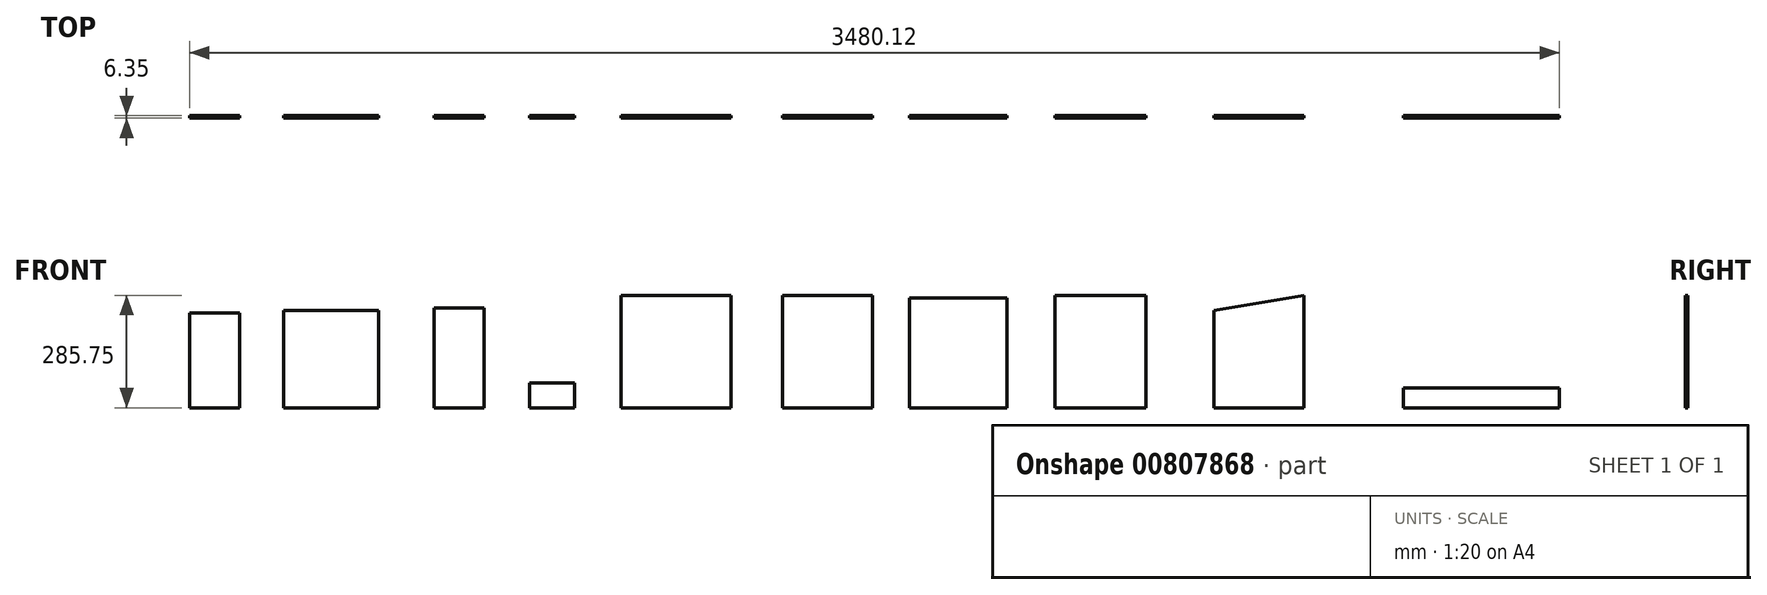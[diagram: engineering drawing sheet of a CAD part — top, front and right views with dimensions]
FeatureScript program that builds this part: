
annotation { "Feature Type Name" : "Feature", "Feature Type Description" : "" }
export const myFeature = defineFeature(function(context is Context, id is Id, definition is map)
    precondition{}
    {
        {
            var Q0;
            Q0=qCreatedBy(makeId("Front.planeOp"),FACE);
            var sketch = newSketch(context, id + "F0", { "sketchPlane" : qUnion([Q0])});
            skLineSegment(sketch, "E0.bottom", {"start": v(-480.49, 172.68) * mm, "end": v(-353.49, 172.68) * mm});
            skLineSegment(sketch, "E0.top", {"start": v(-480.49, -68.62) * mm, "end": v(-353.49, -68.62) * mm});
            skLineSegment(sketch, "E0.left", {"start": v(-480.49, 172.68) * mm, "end": v(-480.49, -68.62) * mm});
            skLineSegment(sketch, "E0.right", {"start": v(-353.49, 172.68) * mm, "end": v(-353.49, -68.62) * mm});
            skLineSegment(sketch, "E1.bottom", {"start": v(-241.3, 179.03) * mm, "end": v(0, 179.03) * mm});
            skLineSegment(sketch, "E1.top", {"start": v(-241.3, -68.62) * mm, "end": v(0, -68.62) * mm});
            skLineSegment(sketch, "E1.left", {"start": v(-241.3, 179.03) * mm, "end": v(-241.3, -68.62) * mm});
            skLineSegment(sketch, "E1.right", {"start": v(0, 179.03) * mm, "end": v(0, -68.62) * mm});
            skLineSegment(sketch, "E2.bottom", {"start": v(141.02, 185.38) * mm, "end": v(268.02, 185.38) * mm});
            skLineSegment(sketch, "E2.top", {"start": v(141.02, -68.62) * mm, "end": v(268.02, -68.62) * mm});
            skLineSegment(sketch, "E2.left", {"start": v(141.02, 185.38) * mm, "end": v(141.02, -68.62) * mm});
            skLineSegment(sketch, "E2.right", {"start": v(268.02, 185.38) * mm, "end": v(268.02, -68.62) * mm});
            skLineSegment(sketch, "E3.bottom", {"start": v(383.19, -68.62) * mm, "end": v(497.49, -68.62) * mm});
            skLineSegment(sketch, "E3.top", {"start": v(383.19, -5.12) * mm, "end": v(497.49, -5.12) * mm});
            skLineSegment(sketch, "E3.left", {"start": v(383.19, -68.62) * mm, "end": v(383.19, -5.12) * mm});
            skLineSegment(sketch, "E3.right", {"start": v(497.49, -68.62) * mm, "end": v(497.49, -5.12) * mm});
            skLineSegment(sketch, "E4.bottom", {"start": v(615.22, 217.13) * mm, "end": v(894.62, 217.13) * mm});
            skLineSegment(sketch, "E4.top", {"start": v(615.22, -68.62) * mm, "end": v(894.62, -68.62) * mm});
            skLineSegment(sketch, "E4.left", {"start": v(615.22, 217.13) * mm, "end": v(615.22, -68.62) * mm});
            skLineSegment(sketch, "E4.right", {"start": v(894.62, 217.13) * mm, "end": v(894.62, -68.62) * mm});
            skLineSegment(sketch, "E5.bottom", {"start": v(1026.44, 217.13) * mm, "end": v(1255.04, 217.13) * mm});
            skLineSegment(sketch, "E5.top", {"start": v(1026.44, -68.62) * mm, "end": v(1255.04, -68.62) * mm});
            skLineSegment(sketch, "E5.left", {"start": v(1026.44, 217.13) * mm, "end": v(1026.44, -68.62) * mm});
            skLineSegment(sketch, "E5.right", {"start": v(1255.04, 217.13) * mm, "end": v(1255.04, -68.62) * mm});
            skLineSegment(sketch, "E6.bottom", {"start": v(1347.93, 210.78) * mm, "end": v(1595.58, 210.78) * mm});
            skLineSegment(sketch, "E6.top", {"start": v(1347.93, -68.62) * mm, "end": v(1595.58, -68.62) * mm});
            skLineSegment(sketch, "E6.left", {"start": v(1347.93, 210.78) * mm, "end": v(1347.93, -68.62) * mm});
            skLineSegment(sketch, "E6.right", {"start": v(1595.58, 210.78) * mm, "end": v(1595.58, -68.62) * mm});
            skLineSegment(sketch, "E7.bottom", {"start": v(1717.51, 217.13) * mm, "end": v(1949.29, 217.13) * mm});
            skLineSegment(sketch, "E7.top", {"start": v(1717.51, -68.62) * mm, "end": v(1949.29, -68.62) * mm});
            skLineSegment(sketch, "E7.left", {"start": v(1717.51, 217.13) * mm, "end": v(1717.51, -68.62) * mm});
            skLineSegment(sketch, "E7.right", {"start": v(1949.29, 217.13) * mm, "end": v(1949.29, -68.62) * mm});
            skLineSegment(sketch, "E8.top", {"start": v(2121.79, -68.62) * mm, "end": v(2350.39, -68.62) * mm});
            skLineSegment(sketch, "E8.left", {"start": v(2121.79, 179.03) * mm, "end": v(2121.79, -68.62) * mm});
            skLineSegment(sketch, "E8.right", {"start": v(2350.39, 217.13) * mm, "end": v(2350.39, -68.62) * mm});
            skLineSegment(sketch, "E9", {"start": v(2121.79, -68.62) * mm, "end": v(2121.79, 179.03) * mm, "construction": true});
            skLineSegment(sketch, "E10", {"start": v(2121.79, 179.03) * mm, "end": v(2350.39, 217.13) * mm});
            skLineSegment(sketch, "E11.bottom", {"start": v(2602.76, -17.82) * mm, "end": v(2999.63, -17.82) * mm});
            skLineSegment(sketch, "E11.top", {"start": v(2602.76, -68.62) * mm, "end": v(2999.63, -68.62) * mm});
            skLineSegment(sketch, "E11.left", {"start": v(2602.76, -17.82) * mm, "end": v(2602.76, -68.62) * mm});
            skLineSegment(sketch, "E11.right", {"start": v(2999.63, -17.82) * mm, "end": v(2999.63, -68.62) * mm});
            skSolve(sketch);
        }
        {
            var Q0;
            Q0 = qSketchRegion(id + "F0", true);
            extrude(context, id + "F1", {"entities" : qUnion([Q0]), "depth" : 6.35 * mm, "offsetDistance" : 25.4 * mm});
        }
    });
